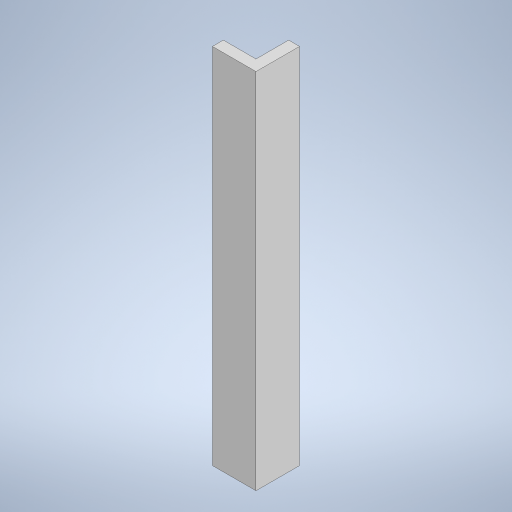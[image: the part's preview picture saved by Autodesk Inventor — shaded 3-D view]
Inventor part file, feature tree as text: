
AUTODESK INVENTOR PART (.ipt)
format: ipt  version: 2023 (Build 270158000, 158)  size: 224,768 bytes
history: native  units: mm
features: extrude x1, sketch x1
ambient origin geometry x8: Origin, YZ Plane, XZ Plane, XY Plane, X Axis, Y Axis, Z Axis, Center Point
bodies: Solid1 (feature_tree)
feature tree (2):
  extrude  "Extrusion1"  Depth=60.0mm
  sketch  "Sketch1"  dims[d0=60.0mm d1=60.0mm d2=15.0mm d3=15.0mm d4=500.0mm d5=0.0mm]
